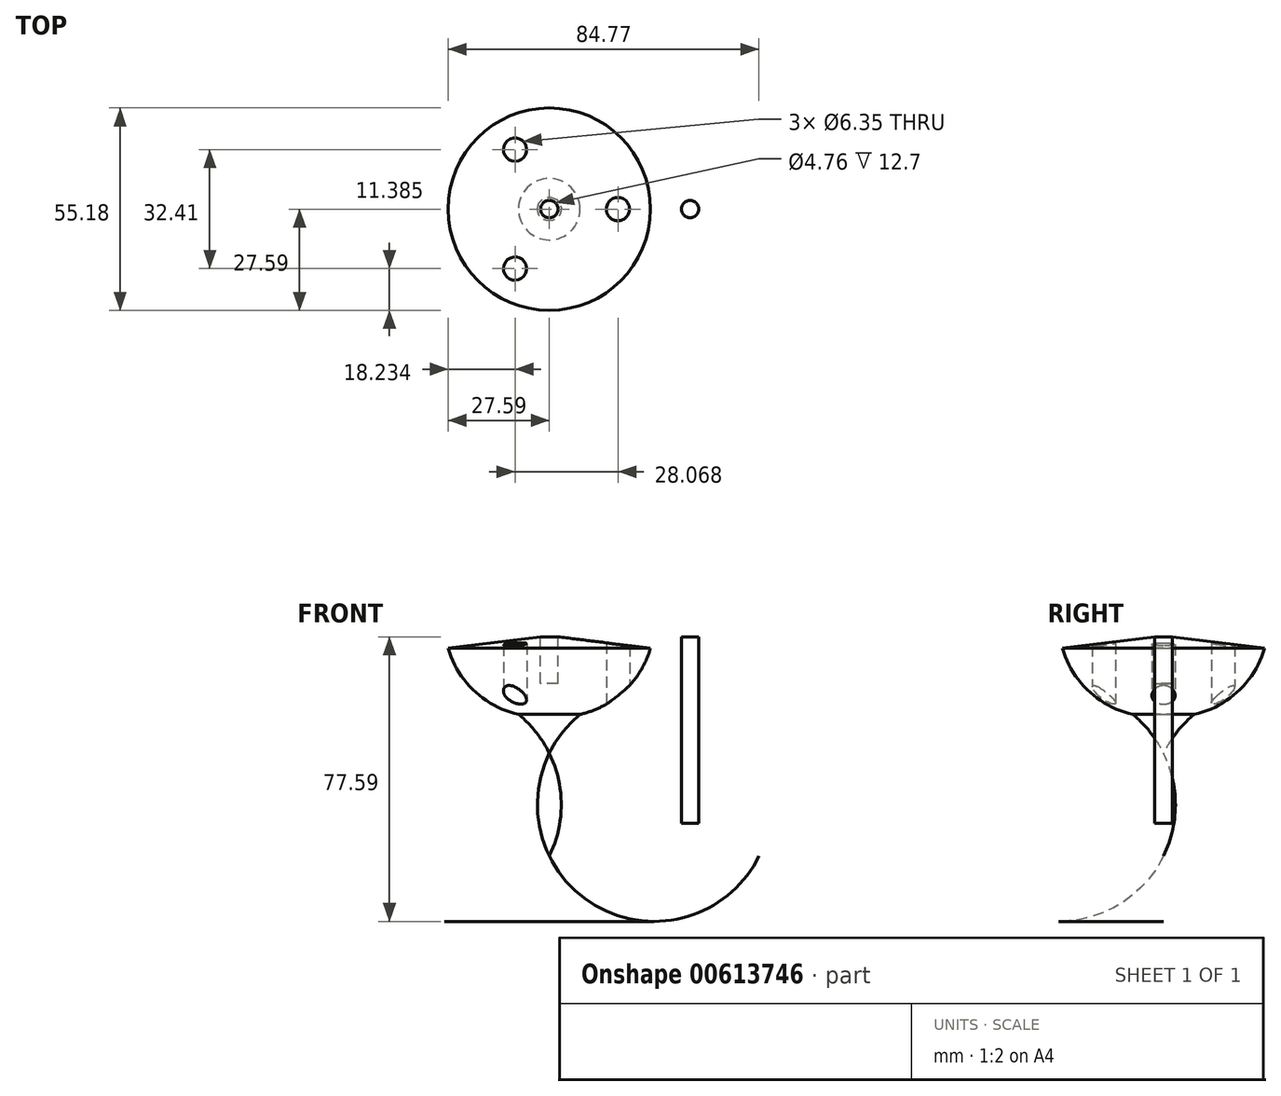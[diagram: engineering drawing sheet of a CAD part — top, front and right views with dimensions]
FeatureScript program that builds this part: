
annotation { "Feature Type Name" : "Feature", "Feature Type Description" : "" }
export const myFeature = defineFeature(function(context is Context, id is Id, definition is map)
    precondition{}
    {
        {
            var Q0;
            Q0=qCreatedBy(makeId("Front.planeOp"),FACE);
            var sketch = newSketch(context, id + "F0", { "sketchPlane" : qUnion([Q0])});
            skLineSegment(sketch, "E0", {"start": v(0, 0) * mm, "end": v(0, 19.05) * mm});
            skLineSegment(sketch, "E1", {"start": v(2.38, 31.75) * mm, "end": v(27.59, 28.6) * mm});
            skArc(sketch, "E2", {"start": v(8.39, 10.6) * mm, "mid": v(3.63, 5.75) * mm, "end": v(0, 0) * mm});
            skArc(sketch, "E3", {"start": v(8.39, 10.6) * mm, "mid": v(20.43, 17) * mm, "end": v(27.59, 28.6) * mm});
            skLineSegment(sketch, "E4", {"start": v(0, 19.05) * mm, "end": v(0, 0) * mm});
            skLineSegment(sketch, "E5", {"start": v(2.38, 31.75) * mm, "end": v(2.38, 19.05) * mm});
            skLineSegment(sketch, "E6", {"start": v(2.38, 19.05) * mm, "end": v(0, 19.05) * mm});
            skSolve(sketch);
        }
        {
            var Q0;
            Q0=makeQuery(id+"F0.imprint","IMPRINT",FACE,{"disambiguationData":[TD([[makeQuery(id+"F0.imprint","IMPRINT",EDGE,{"derivedFrom":sQuery(id+"F0.wireOp",EDGE,"15uGU3SM-u4RD-X9Ay-JVqv-ALSxTrI4hlsa")}),-1.0]])]});
            var Q1;
            Q1=makeQuery(id+"F0.imprint","IMPRINT",FACE,{"disambiguationData":[TD([[makeQuery(id+"F0.imprint","IMPRINT",EDGE,{"derivedFrom":sQuery(id+"F0.wireOp",EDGE,"E1")}),-1.0]])]});
            var Q2;
            Q2=sQuery(id+"F0.wireOp",EDGE,"E4");
            revolve(context, id + "F1", {"entities" : qUnion([Q0, Q1]), "axis" : qUnion([Q2]), "revolveType" : RevolveType.FULL});
        }
        {
            var Q0;
            Q0=qCreatedBy(makeId("Top.planeOp"),FACE);
            var sketch = newSketch(context, id + "F2", { "sketchPlane" : qUnion([Q0])});
            skCircle(sketch, "E7", {"center": v(18.71, 0) * mm, "radius": 3.18 * mm});
            skCircle(sketch, "E8", {"center": v(0, 0) * mm, "radius": 18.71 * mm});
            skCircle(sketch, "E9.1.0", {"center": v(-9.36, 16.2) * mm, "radius": 3.18 * mm});
            skCircle(sketch, "E9.2.0", {"center": v(-9.36, -16.2) * mm, "radius": 3.18 * mm});
            skSolve(sketch);
        }
        {
            var Q0;
            Q0=sQuery(id+"F2.wireOp",VERTEX,"E7.center");
            var Q1;
            Q1=sQuery(id+"F2.wireOp",VERTEX,"E9.1.0.center");
            var Q2;
            Q2=sQuery(id+"F2.wireOp",VERTEX,"E9.2.0.center");
            var Q3;
            Q3=makeQuery(id+"F1.opRevolve","SWEPT_BODY",BODY,{"disambiguationData":[OSD([sQuery(id+"F0.wireOp",EDGE,"15uGU3SM-u4RD-X9Ay-JVqv-ALSxTrI4hlsa"),sQuery(id+"F0.wireOp",EDGE,"5JsyrMfI-APAh-AfAA-ZDuw-GzcSQfAlMaNL"),sQuery(id+"F0.wireOp",EDGE,"E1"),sQuery(id+"F0.wireOp",EDGE,"E2"),sQuery(id+"F0.wireOp",EDGE,"E3"),sQuery(id+"F0.wireOp",EDGE,"E4")])]});
            hole(context, id + "F3", {"style" : HoleStyle.SIMPLE, "endStyle" : HoleEndStyle.THROUGH, "oppositeDirection" : true, "holeDiameter" : 6.35 * mm, "majorDiameter" : 6.35 * mm, "isTappedThrough" : true, "tappedDepth" : 12.7 * mm, "tapClearance" : 3, "locations" : qUnion([Q0, Q1, Q2]), "scope" : qUnion([Q3])});
        }
        {
            var Q0;
            Q0=qCreatedBy(makeId("Top.planeOp"),FACE);
            var sketch = newSketch(context, id + "F4", { "sketchPlane" : qUnion([Q0])});
            skCircle(sketch, "E10", {"center": v(38.38, 0) * mm, "radius": 2.35 * mm});
            skSolve(sketch);
        }
        {
            var Q0;
            Q0 = qSketchRegion(id + "F4", true);
            extrude(context, id + "F5", {"entities" : qUnion([Q0]), "depth" : 31.75 * mm, "offsetDistance" : 25.4 * mm, "hasSecondDirection" : true, "secondDirectionOppositeDirection" : true, "secondDirectionDepth" : 19.05 * mm});
        }
    });
